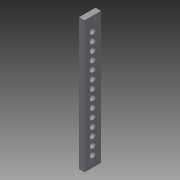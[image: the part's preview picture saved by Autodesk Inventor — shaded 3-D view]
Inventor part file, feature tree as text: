
AUTODESK INVENTOR PART (.ipt)
format: ipt  version: 2014 (Build 180170000, 170)  size: 93,696 bytes
history: native  units: in
note: dims shown in document units (in); Inventor stores cm internally (conversion verified against a paired STEP export)
features: extrude x1, sketch x1
ambient origin geometry x8: Origin, YZ Plane, XZ Plane, XY Plane, X Axis, Y Axis, Z Axis, Center Point
bodies: Solid1 (feature_tree)
feature tree (2):
  extrude  "Extrusion1"  Depth=6.0in
  sketch  "Sketch1"  dims[d0=0.75in d1=6.0in d2=0.25in d3=0.5in d4=0.375in d5=5.5118in d7=0.375in d8=0.3937in d10=1.0in d12=0.25in d13=0.0in]
